# Revit family: БКМ10П_RV17_LOD400 (05.11.23)
name_source: partatom
category: Электрооборудование
revit_build: Autodesk Revit 2017 (Build: 20170118_1100(x64)
units: mm (PartAtom-declared; Revit-internal decimal feet)

## family parameters
Всегда вертикально = Нет
Конфигурация панели = Два столбца, слева направо
На основе рабочей плоскости = Да
Общий = Нет
При загрузке вырезать с полостями = Нет
Размер круглого соединителя = Использовать диаметр
Тип детали = Щит
Точка расчета площади = Нет

## types (1)
- БКМ10П
    ADSK_URL страницы изделия = https://stilsoft.ru
    ADSK_Единица измерения = шт.
    ADSK_Завод-изготовитель = ООО «Основа Безопасности»
    ADSK_Количество = 1
    ADSK_Марка = СТВФ.426471.185
    ADSK_Масса = 3.5
    ADSK_Наименование = Коммутатор БКМ10П
    ADSK_Размер_Высота = 80 мм
    ADSK_Размер_Глубина = 125 мм
    ADSK_Размер_Длина = 270 мм
    d_короба = 20 мм
    Время непрерывной работы, ч = круглосуточно
    Диапазон рабочих температур, °С = от – 40 до + 50
    Количество коммутируемых портов Auto MDI/MDIX с поддержкой РоЕ, шт. = 10
    Количество разъемов, шт.  8P8C = 10
    Количество разъемов, шт.  SFP = 2
    Мощность = 25
    Напряжение электропитания однофазной сети переменного тока, В /Гц = 180-264 / 47-63
    Отметка по умолчанию = 1219 мм
    Потребляемая мощность, не более, Вт = 350
    Рабочая длина волны, нм = 1310 мм
    Расстояние передачи данных (информации), дальность действия по кабелю UTP-5e, м = до 100
    Расстояние передачи данных (информации), дальность действия по оптическому кабелю , м = до 20000
    Скорость передачи данных, Мбит/с Ethernet (8P8C) = 10/100/1000
    Скорость передачи данных, Мбит/с SFP (оптический порт) = 1000
    Стандарт РоЕ = IEEE 802.3 af/at
    Суммарная мощность подключаемых устройств по РоЕ, Вт = 251
    Тип кабеля = SМ 9/125 μm
    Тип разъема = 2xLC
